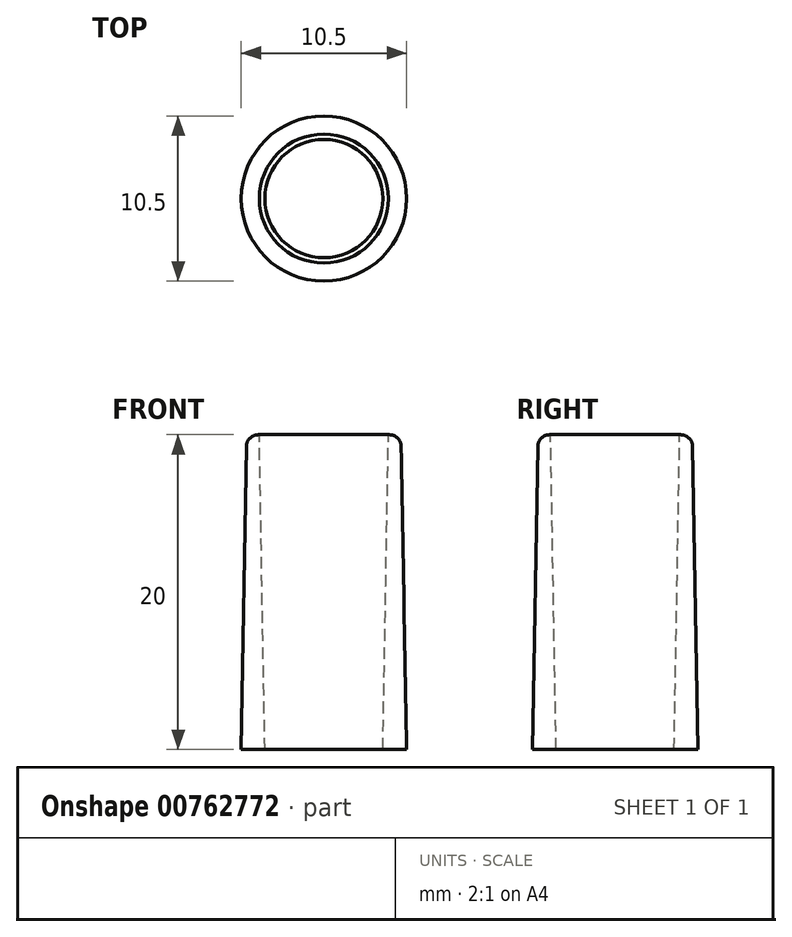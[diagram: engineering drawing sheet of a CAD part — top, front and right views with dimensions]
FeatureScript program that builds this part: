
annotation { "Feature Type Name" : "Feature", "Feature Type Description" : "" }
export const myFeature = defineFeature(function(context is Context, id is Id, definition is map)
    precondition{}
    {
        {
            var Q0;
            Q0=qCreatedBy(makeId("Top.planeOp"),FACE);
            var sketch = newSketch(context, id + "F0", { "sketchPlane" : qUnion([Q0])});
            skCircle(sketch, "E0", {"center": v(0, 0) * mm, "radius": 3.75 * mm});
            skCircle(sketch, "E1.0", {"center": v(0, 0) * mm, "radius": 5.25 * mm});
            skSolve(sketch);
        }
        {
            var Q0;
            Q0 = qSketchRegion(id + "F0", true);
            extrude(context, id + "F1", {"entities" : qUnion([Q0]), "depth" : 20 * mm, "offsetDistance" : 25 * mm, "hasDraft" : true, "draftAngle" : 1 * degree, "draftPullDirection" : true});
        }
        {
            var Q0;
            Q0=makeQuery(id+"F1.opExtrude","CAP_EDGE",EDGE,{"disambiguationData":[OSD([sQuery(id+"F0.wireOp",EDGE,"E1.0")])],"isStart":false});
            fillet(context, id + "F2", {"entities" : qUnion([Q0]), "radius" : .75 * mm, "tangentPropagation" : true, "allowEdgeOverflow" : false});
        }
    });
